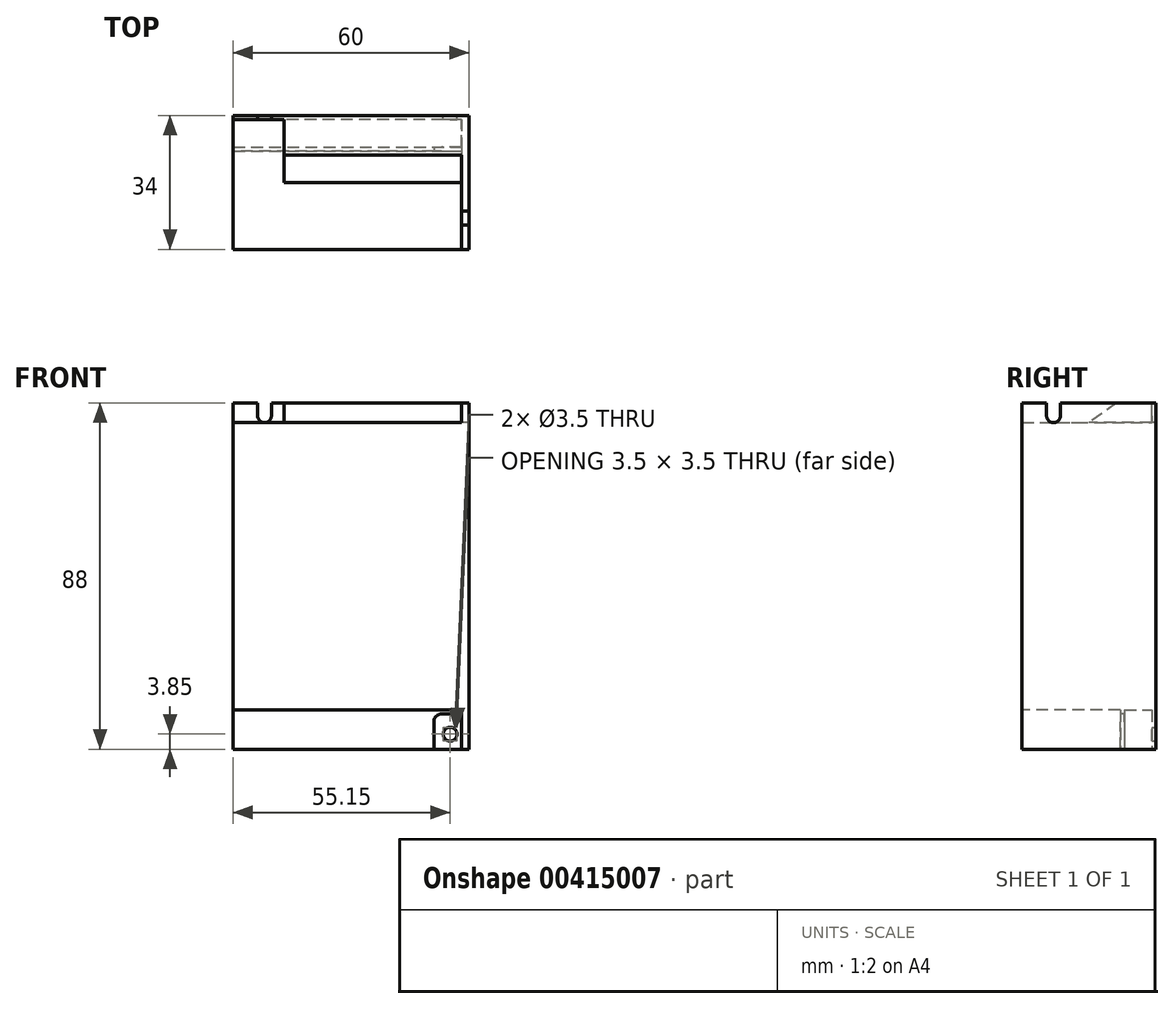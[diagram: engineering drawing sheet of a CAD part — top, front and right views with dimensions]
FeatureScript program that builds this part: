
annotation { "Feature Type Name" : "Feature", "Feature Type Description" : "" }
export const myFeature = defineFeature(function(context is Context, id is Id, definition is map)
    precondition{}
    {
        {
            var Q0;
            Q0=qCreatedBy(makeId("Front.planeOp"),FACE);
            var sketch = newSketch(context, id + "F0", { "sketchPlane" : qUnion([Q0])});
            skLineSegment(sketch, "E0.bottom", {"start": v(30, 44) * mm, "end": v(-30, 44) * mm});
            skLineSegment(sketch, "E0.top", {"start": v(30, -44) * mm, "end": v(-30, -44) * mm});
            skLineSegment(sketch, "E0.left", {"start": v(30, 44) * mm, "end": v(30, -44) * mm});
            skLineSegment(sketch, "E0.right", {"start": v(-30, 44) * mm, "end": v(-30, -44) * mm});
            skPoint(sketch, "E0.middle", {"position": v(0, 0) * mm});
            skSolve(sketch);
        }
        {
            var Q0;
            Q0=makeQuery(id+"F0.imprint","IMPRINT",FACE,{"disambiguationData":[TD([[makeQuery(id+"F0.imprint","IMPRINT",EDGE,{"derivedFrom":sQuery(id+"F0.wireOp",EDGE,"E0.bottom")}),1.0]])]});
            extrude(context, id + "F1", {"entities" : qUnion([Q0]), "depth" : 34 * mm, "offsetDistance" : 25 * mm});
        }
        {
            var Q0;
            Q0=makeQuery(id+"F1.opExtrude","SWEPT_FACE",FACE,{"disambiguationData":[OSD([sQuery(id+"F0.wireOp",EDGE,"E0.right")])]});
            var sketch = newSketch(context, id + "F2", { "sketchPlane" : qUnion([Q0])});
            skLineSegment(sketch, "E1", {"start": v(34, 44) * mm, "end": v(34, 39) * mm});
            skLineSegment(sketch, "E2", {"start": v(34, 39) * mm, "end": v(17, 39) * mm});
            skLineSegment(sketch, "E3", {"start": v(17, 39) * mm, "end": v(10, 44) * mm});
            skSolve(sketch);
        }
        {
            var Q0;
            {var subQ0=sQuery(id+"F2.wireOp",EDGE,"E1");Q0=makeQuery(id+"F2.imprint","IMPRINT",FACE,{"disambiguationData":[TD([[makeQuery(id+"F2.imprint","IMPRINT",EDGE,{"derivedFrom":subQ0}),-1.0]])]});}
            extrude(context, id + "F3", {"entities" : qUnion([Q0]), "operationType" : NewBodyOperationType.REMOVE, "oppositeDirection" : true, "depth" : 58 * mm});
        }
        {
            var Q0;
            Q0=makeQuery(id+"F1.opExtrude","CAP_FACE",FACE,{"disambiguationData":[OSD([sQuery(id+"F0.wireOp",EDGE,"E0.bottom"),sQuery(id+"F0.wireOp",EDGE,"E0.top"),sQuery(id+"F0.wireOp",EDGE,"E0.left"),sQuery(id+"F0.wireOp",EDGE,"E0.right")])],"isStart":false});
            var sketch = newSketch(context, id + "F4", { "sketchPlane" : qUnion([Q0])});
            skLineSegment(sketch, "E4.0", {"start": v(28, 44) * mm, "end": v(-30, 44) * mm});
            skLineSegment(sketch, "E5.0", {"start": v(-30, 39) * mm, "end": v(-30, 44) * mm});
            skLineSegment(sketch, "E6", {"start": v(-30, 44) * mm, "end": v(-17, 44) * mm});
            skLineSegment(sketch, "E7", {"start": v(-17, 44) * mm, "end": v(-17, 39) * mm});
            skLineSegment(sketch, "E8", {"start": v(-30, -34) * mm, "end": v(28, -34) * mm});
            skLineSegment(sketch, "E9", {"start": v(28, -34) * mm, "end": v(28, -44) * mm});
            skSolve(sketch);
        }
        {
            var Q0;
            {var subQ0=sQuery(id+"F4.wireOp",EDGE,"E5.0");Q0=makeQuery(id+"F4.imprint","IMPRINT",FACE,{"disambiguationData":[TD([[makeQuery(id+"F4.imprint","IMPRINT",EDGE,{"derivedFrom":subQ0}),-1.0]])]});}
            extrude(context, id + "F5", {"entities" : qUnion([Q0]), "operationType" : NewBodyOperationType.REMOVE, "oppositeDirection" : true, "depth" : 33 * mm});
        }
        {
            var Q0;
            Q0=makeQuery(id+"F5.boolean.opBoolean","COPY",FACE,{"derivedFrom":makeQuery(id+"F5.opExtrude","CAP_FACE",FACE,{"disambiguationData":[OSD([sQuery(id+"F0.wireOp",EDGE,"E0.right"),sQuery(id+"F2.wireOp",EDGE,"E1"),sQuery(id+"F2.wireOp",EDGE,"E2"),sQuery(id+"F4.wireOp",EDGE,"E5.0"),sQuery(id+"F4.wireOp",EDGE,"E6"),sQuery(id+"F4.wireOp",EDGE,"E7")])],"isStart":false})});
            var sketch = newSketch(context, id + "F6", { "sketchPlane" : qUnion([Q0])});
            skArc(sketch, "E10", {"start": v(-23.75, 40.7) * mm, "mid": v(-21.98, 39) * mm, "end": v(-20.25, 40.75) * mm});
            skLineSegment(sketch, "E11", {"start": v(-23.75, 40.7) * mm, "end": v(-23.83, 44) * mm});
            skLineSegment(sketch, "E12", {"start": v(-20.25, 40.75) * mm, "end": v(-20.25, 44) * mm});
            skSolve(sketch);
        }
        {
            var Q0;
            {var subQ1=sQuery(id+"F6.wireOp",EDGE,"E11");Q0=makeQuery(id+"F6.imprint","IMPRINT",FACE,{"disambiguationData":[TD([[makeQuery(id+"F6.imprint","IMPRINT",EDGE,{"derivedFrom":subQ1}),-1.0]])]});}
            extrude(context, id + "F7", {"entities" : qUnion([Q0]), "operationType" : NewBodyOperationType.REMOVE, "endBound" : BoundingType.THROUGH_ALL, "oppositeDirection" : true, "depth" : 25 * mm});
        }
        {
            var Q0;
            Q0=makeQuery(id+"F3.boolean.opBoolean","COPY",FACE,{"derivedFrom":makeQuery(id+"F3.opExtrude","CAP_FACE",FACE,{"disambiguationData":[OSD([sQuery(id+"F0.wireOp",EDGE,"E0.bottom"),sQuery(id+"F0.wireOp",EDGE,"E0.right"),sQuery(id+"F2.wireOp",EDGE,"E1"),sQuery(id+"F2.wireOp",EDGE,"E2"),sQuery(id+"F2.wireOp",EDGE,"E3")])],"isStart":false})});
            var sketch = newSketch(context, id + "F8", { "sketchPlane" : qUnion([Q0])});
            skArc(sketch, "E13", {"start": v(24.25, 40.75) * mm, "mid": v(26, 39) * mm, "end": v(27.75, 40.75) * mm});
            skLineSegment(sketch, "E14", {"start": v(27.75, 40.75) * mm, "end": v(27.75, 44) * mm});
            skLineSegment(sketch, "E15", {"start": v(24.25, 40.75) * mm, "end": v(24.25, 44) * mm});
            skSolve(sketch);
        }
        {
            var Q0;
            {var subQ1=sQuery(id+"F8.wireOp",EDGE,"E14");Q0=makeQuery(id+"F8.imprint","IMPRINT",FACE,{"disambiguationData":[TD([[makeQuery(id+"F8.imprint","IMPRINT",EDGE,{"derivedFrom":subQ1}),1.0]])]});}
            extrude(context, id + "F9", {"entities" : qUnion([Q0]), "operationType" : NewBodyOperationType.REMOVE, "endBound" : BoundingType.THROUGH_ALL, "oppositeDirection" : true, "depth" : 25 * mm});
        }
        {
            var Q0;
            {var subQ0=sQuery(id+"F4.wireOp",EDGE,"E8");Q0=makeQuery(id+"F4.imprint","IMPRINT",FACE,{"disambiguationData":[TD([[makeQuery(id+"F4.imprint","IMPRINT",EDGE,{"derivedFrom":subQ0}),-1.0]])]});}
            extrude(context, id + "F10", {"entities" : qUnion([Q0]), "operationType" : NewBodyOperationType.REMOVE, "oppositeDirection" : true, "depth" : 25 * mm});
        }
        {
            var Q0;
            Q0=makeQuery(id+"F1.opExtrude","SWEPT_FACE",FACE,{"disambiguationData":[OSD([sQuery(id+"F0.wireOp",EDGE,"E0.top")])]});
            var sketch = newSketch(context, id + "F11", { "sketchPlane" : qUnion([Q0])});
            skLineSegment(sketch, "E16", {"start": v(-30, 8) * mm, "end": v(28, 8) * mm});
            skLineSegment(sketch, "E17", {"start": v(28, 8) * mm, "end": v(28, 1) * mm});
            skLineSegment(sketch, "E18", {"start": v(28, 1) * mm, "end": v(-30, 1) * mm});
            skLineSegment(sketch, "E19", {"start": v(-30, 1) * mm, "end": v(-30, 8) * mm});
            skSolve(sketch);
        }
        {
            var Q0;
            Q0=makeQuery(id+"F11.imprint","IMPRINT",FACE,{"disambiguationData":[TD([[makeQuery(id+"F11.imprint","IMPRINT",EDGE,{"derivedFrom":sQuery(id+"F11.wireOp",EDGE,"E16")}),-1.0]])]});
            extrude(context, id + "F12", {"entities" : qUnion([Q0]), "operationType" : NewBodyOperationType.REMOVE, "oppositeDirection" : true, "depth" : 10 * mm});
        }
        {
            var Q0;
            Q0=makeQuery(id+"F10.boolean.opBoolean","COPY",FACE,{"derivedFrom":makeQuery(id+"F10.opExtrude","CAP_FACE",FACE,{"disambiguationData":[OSD([sQuery(id+"F0.wireOp",EDGE,"E0.top"),sQuery(id+"F0.wireOp",EDGE,"E0.right"),sQuery(id+"F4.wireOp",EDGE,"E8"),sQuery(id+"F4.wireOp",EDGE,"E9")])],"isStart":false})});
            var sketch = newSketch(context, id + "F13", { "sketchPlane" : qUnion([Q0])});
            skLineSegment(sketch, "E20", {"start": v(21, -44) * mm, "end": v(21, -37) * mm});
            skLineSegment(sketch, "E21", {"start": v(23, -35) * mm, "end": v(28, -35) * mm});
            skPoint(sketch, "E22.visualSharp", {"position": v(21, -35) * mm});
            skArc(sketch, "E22.filletArc", {"start": v(23, -35) * mm, "mid": v(21.59, -35.59) * mm, "end": v(21, -37) * mm});
            skSolve(sketch);
        }
        {
            var Q0;
            {var subQ4=sQuery(id+"F13.wireOp",EDGE,"E20");Q0=makeQuery(id+"F13.imprint","IMPRINT",FACE,{"disambiguationData":[TD([[makeQuery(id+"F13.imprint","IMPRINT",EDGE,{"derivedFrom":subQ4}),-1.0]])]});}
            extrude(context, id + "F14", {"entities" : qUnion([Q0]), "operationType" : NewBodyOperationType.REMOVE, "oppositeDirection" : true, "depth" : 3 * mm});
        }
        {
            var Q0;
            Q0=makeQuery(id+"F1.opExtrude","CAP_FACE",FACE,{"disambiguationData":[OSD([sQuery(id+"F0.wireOp",EDGE,"E0.bottom"),sQuery(id+"F0.wireOp",EDGE,"E0.top"),sQuery(id+"F0.wireOp",EDGE,"E0.left"),sQuery(id+"F0.wireOp",EDGE,"E0.right")])],"isStart":true});
            var sketch = newSketch(context, id + "F15", { "sketchPlane" : qUnion([Q0])});
            skCircle(sketch, "E23", {"center": v(-25.15, -40.15) * mm, "radius": 1.75 * mm});
            skSolve(sketch);
        }
        {
            var Q0;
            Q0=makeQuery(id+"F15.imprint","IMPRINT",FACE,{"disambiguationData":[TD([[makeQuery(id+"F15.imprint","IMPRINT",EDGE,{"derivedFrom":sQuery(id+"F15.wireOp",EDGE,"E23")}),1.0]])]});
            extrude(context, id + "F16", {"entities" : qUnion([Q0]), "operationType" : NewBodyOperationType.REMOVE, "oppositeDirection" : true, "depth" : 3 * mm});
        }
    });
